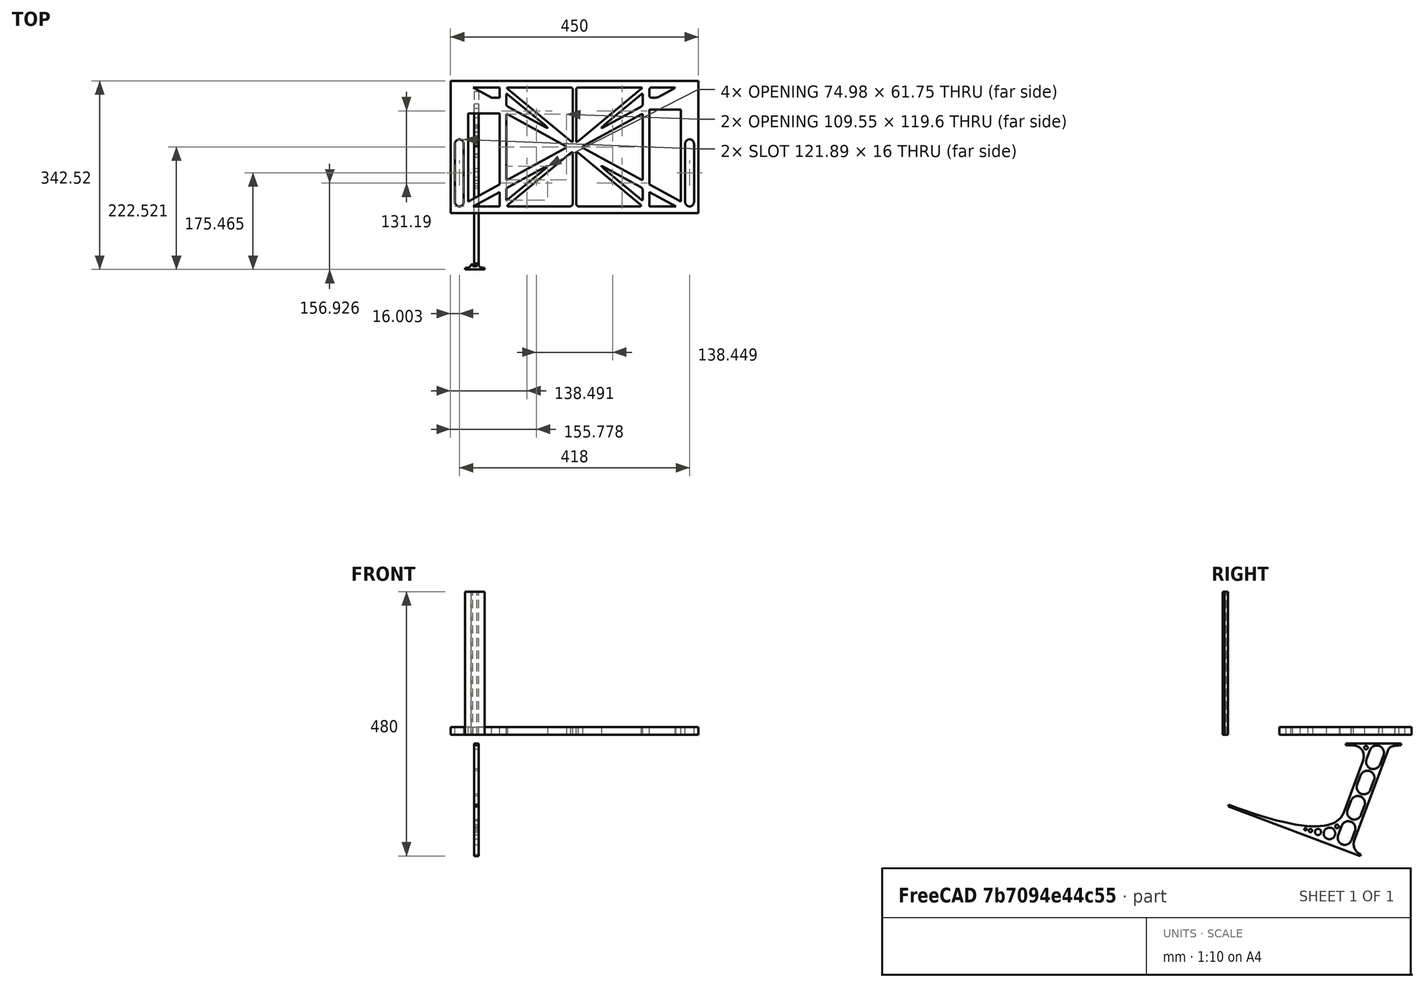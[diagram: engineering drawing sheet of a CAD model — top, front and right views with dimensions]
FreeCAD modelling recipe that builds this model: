
FCSTD DOCUMENT  (FreeCAD 0.19R0.19.2)
Label: laptopStand100
License: All rights reserved
LicenseURL: http://en.wikipedia.org/wiki/All_rights_reserved
objects: Sketcher::SketchObject×3, Part::Extrusion×3
note: 6 computed .brp shape members not serialized (recipe doc carries the construction recipe); baked Part::Feature solids carry a one-line shape summary decoded from their .brp

FEATURE [Sketcher::SketchObject] Sketch
  FullyConstrained = false
  sketch-geometry (276):
    g0: LineSegment StartX=-10.9272 StartY=-82.7794 StartZ=0 EndX=46.0728 EndY=-51.4823 EndZ=0
    g1: LineSegment StartX=366.073 StartY=-91.7794 StartZ=0 EndX=318.073 EndY=-65.424 EndZ=0
    g2: LineSegment StartX=-10.9272 StartY=77.3346 StartZ=0 EndX=-10.9272 EndY=-82.7794 EndZ=0
    g3: LineSegment StartX=375.073 StartY=-82.7794 StartZ=0 EndX=375.073 EndY=83.9235 EndZ=0
    g4: LineSegment StartX=-1.92719 StartY=-91.7794 StartZ=0 EndX=46.0728 EndY=-91.7794 EndZ=0
    g5: LineSegment StartX=318.073 StartY=83.9235 StartZ=0 EndX=318.073 EndY=-51.4823 EndZ=0
    g6: LineSegment StartX=318.073 StartY=-51.4823 StartZ=0 EndX=375.073 EndY=-82.7794 EndZ=0
    g7: LineSegment StartX=318.073 StartY=-65.424 StartZ=0 EndX=318.073 EndY=-91.7794 EndZ=0
    g8: LineSegment StartX=318.073 StartY=-91.7794 StartZ=0 EndX=366.073 EndY=-91.7794 EndZ=0
    g9: LineSegment StartX=46.0728 StartY=-65.424 StartZ=0 EndX=-1.92719 EndY=-91.7794 EndZ=0
    g10: LineSegment StartX=46.0728 StartY=-65.424 StartZ=0 EndX=46.0728 EndY=-91.7794 EndZ=0
    g11: LineSegment StartX=46.0728 StartY=77.3346 StartZ=0 EndX=46.0728 EndY=-51.4823 EndZ=0
    g12: LineSegment StartX=-42.9272 StartY=136.221 StartZ=0 EndX=-42.9272 EndY=-103.779 EndZ=0
    g13: LineSegment StartX=407.073 StartY=136.221 StartZ=0 EndX=407.073 EndY=-103.779 EndZ=0
    g14: ArcOfCircle CenterX=-26.9272 CenterY=22.1087 CenterZ=0 NormalX=0 NormalY=0 NormalZ=1 AngleXU=0 Radius=8 StartAngle=1e-16 EndAngle=3.14159
    g15: ArcOfCircle CenterX=-26.9272 CenterY=-83.7794 CenterZ=0 NormalX=0 NormalY=0 NormalZ=1 AngleXU=0 Radius=8 StartAngle=3.14159 EndAngle=6.28319
    g16: LineSegment StartX=-34.9272 StartY=22.1087 StartZ=0 EndX=-34.9272 EndY=-83.7794 EndZ=0
    g17: LineSegment StartX=-18.9272 StartY=22.1087 StartZ=0 EndX=-18.9272 EndY=-83.7794 EndZ=0
    g18: ArcOfCircle CenterX=391.073 CenterY=22.1087 CenterZ=0 NormalX=0 NormalY=0 NormalZ=1 AngleXU=0 Radius=8 StartAngle=-4.4e-15 EndAngle=3.14159
    g19: LineSegment StartX=399.073 StartY=22.1087 StartZ=0 EndX=399.073 EndY=-83.7794 EndZ=0
    g20: LineSegment StartX=383.073 StartY=22.1087 StartZ=0 EndX=383.073 EndY=-83.7794 EndZ=0
    g21: ArcOfCircle CenterX=391.073 CenterY=-83.7794 CenterZ=0 NormalX=0 NormalY=0 NormalZ=1 AngleXU=0 Radius=8 StartAngle=3.14159 EndAngle=6.28319
    g22: Circle CenterX=175.022 CenterY=27.0628 CenterZ=0 NormalX=0 NormalY=0 NormalZ=1 AngleXU=0 Radius=1
    g23: Circle CenterX=179.022 CenterY=24.8665 CenterZ=0 NormalX=0 NormalY=0 NormalZ=1 AngleXU=0 Radius=1
    g24: Circle CenterX=179.022 CenterY=27.0628 CenterZ=0 NormalX=0 NormalY=0 NormalZ=1 AngleXU=0 Radius=1
    g25: BSplineCurve PolesCount=3 KnotsCount=2 Degree=2 IsPeriodic=0
    g26: GeomPoint X=175.022 Y=27.0628 Z=0
    g27: GeomPoint X=179.022 Y=27.0628 Z=0
    g28: Circle CenterX=189.124 CenterY=27.0628 CenterZ=0 NormalX=0 NormalY=0 NormalZ=1 AngleXU=0 Radius=1
    g29: Circle CenterX=185.124 CenterY=24.8665 CenterZ=0 NormalX=0 NormalY=0 NormalZ=1 AngleXU=0 Radius=1
    g30: Circle CenterX=185.124 CenterY=27.0628 CenterZ=0 NormalX=0 NormalY=0 NormalZ=1 AngleXU=0 Radius=1
    g31: BSplineCurve PolesCount=3 KnotsCount=2 Degree=2 IsPeriodic=0
    g32: GeomPoint X=189.124 Y=27.0628 Z=0
    g33: GeomPoint X=185.124 Y=27.0628 Z=0
    g34: Circle CenterX=175.022 CenterY=5.37834 CenterZ=0 NormalX=0 NormalY=0 NormalZ=1 AngleXU=0 Radius=1
    g35: Circle CenterX=179.022 CenterY=7.57463 CenterZ=0 NormalX=0 NormalY=0 NormalZ=1 AngleXU=0 Radius=1
    g36: Circle CenterX=179.022 CenterY=5.34704 CenterZ=0 NormalX=0 NormalY=0 NormalZ=1 AngleXU=0 Radius=1
    g37: BSplineCurve PolesCount=3 KnotsCount=2 Degree=2 IsPeriodic=0
    g38: GeomPoint X=175.022 Y=5.37834 Z=0
    g39: GeomPoint X=179.022 Y=5.34704 Z=0
    g40: Circle CenterX=189.124 CenterY=5.37834 CenterZ=0 NormalX=0 NormalY=0 NormalZ=1 AngleXU=0 Radius=1
    g41: Circle CenterX=185.124 CenterY=7.57463 CenterZ=0 NormalX=0 NormalY=0 NormalZ=1 AngleXU=0 Radius=1
    g42: Circle CenterX=185.124 CenterY=5.34704 CenterZ=0 NormalX=0 NormalY=0 NormalZ=1 AngleXU=0 Radius=1
    g43: BSplineCurve PolesCount=3 KnotsCount=2 Degree=2 IsPeriodic=0
    g44: GeomPoint X=189.124 Y=5.37834 Z=0
    g45: GeomPoint X=185.124 Y=5.34704 Z=0
    g46: Circle CenterX=165.871 CenterY=18.1458 CenterZ=0 NormalX=0 NormalY=0 NormalZ=1 AngleXU=0 Radius=1
    g47: Circle CenterX=169.377 CenterY=16.2206 CenterZ=0 NormalX=0 NormalY=0 NormalZ=1 AngleXU=0 Radius=1
    g48: Circle CenterX=165.871 CenterY=14.2954 CenterZ=0 NormalX=0 NormalY=0 NormalZ=1 AngleXU=0 Radius=1
    g49: BSplineCurve PolesCount=3 KnotsCount=2 Degree=2 IsPeriodic=0
    g50: GeomPoint X=165.871 Y=18.1458 Z=0
    g51: GeomPoint X=165.871 Y=14.2954 Z=0
    g52: Circle CenterX=198.275 CenterY=18.1458 CenterZ=0 NormalX=0 NormalY=0 NormalZ=1 AngleXU=0 Radius=1
    g53: Circle CenterX=194.768 CenterY=16.2206 CenterZ=0 NormalX=0 NormalY=0 NormalZ=1 AngleXU=0 Radius=1
    g54: Circle CenterX=198.275 CenterY=14.2954 CenterZ=0 NormalX=0 NormalY=0 NormalZ=1 AngleXU=0 Radius=1
    g55: BSplineCurve PolesCount=3 KnotsCount=2 Degree=2 IsPeriodic=0
    g56: GeomPoint X=198.275 Y=18.1458 Z=0
    g57: GeomPoint X=198.275 Y=14.2954 Z=0
    g58: LineSegment StartX=407.073 StartY=-103.779 StartZ=0 EndX=-42.9272 EndY=-103.779 EndZ=0
    g59: LineSegment StartX=407.073 StartY=136.221 StartZ=0 EndX=-42.9272 EndY=136.221 EndZ=0
    g60: LineSegment StartX=46.0728 StartY=77.3346 StartZ=0 EndX=-10.9272 EndY=77.3346 EndZ=0
    g61: LineSegment StartX=46.0728 StartY=105.865 StartZ=0 EndX=31.5028 EndY=105.865 EndZ=0
    g62: LineSegment StartX=46.0728 StartY=124.221 StartZ=0 EndX=46.0728 EndY=105.865 EndZ=0
    g63: LineSegment StartX=-1.92719 StartY=124.221 StartZ=0 EndX=31.5028 EndY=105.865 EndZ=0
    g64: LineSegment StartX=46.0728 StartY=124.221 StartZ=0 EndX=-1.92719 EndY=124.221 EndZ=0
    g65: LineSegment StartX=318.073 StartY=83.9235 StartZ=0 EndX=375.073 EndY=83.9235 EndZ=0
    g66: Circle CenterX=125.607 CenterY=54.1951 CenterZ=0 NormalX=0 NormalY=0 NormalZ=1 AngleXU=0 Radius=1
    g67: Circle CenterX=139.632 CenterY=46.4944 CenterZ=0 NormalX=0 NormalY=0 NormalZ=1 AngleXU=0 Radius=1
    g68: Circle CenterX=127.326 CenterY=56.7187 CenterZ=0 NormalX=0 NormalY=0 NormalZ=1 AngleXU=0 Radius=1
    g69: BSplineCurve PolesCount=3 KnotsCount=2 Degree=2 IsPeriodic=0
    g70: GeomPoint X=125.607 Y=54.1951 Z=0
    g71: GeomPoint X=127.326 Y=56.7187 Z=0
    g72: Circle CenterX=236.821 CenterY=56.7187 CenterZ=0 NormalX=0 NormalY=0 NormalZ=1 AngleXU=0 Radius=1
    g73: Circle CenterX=224.513 CenterY=46.4944 CenterZ=0 NormalX=0 NormalY=0 NormalZ=1 AngleXU=0 Radius=1
    g74: Circle CenterX=238.538 CenterY=54.1951 CenterZ=0 NormalX=0 NormalY=0 NormalZ=1 AngleXU=0 Radius=1
    g75: BSplineCurve PolesCount=3 KnotsCount=2 Degree=2 IsPeriodic=0
    g76: GeomPoint X=236.821 Y=56.7187 Z=0
    g77: GeomPoint X=238.538 Y=54.1951 Z=0
    g78: Circle CenterX=238.538 CenterY=-21.7539 CenterZ=0 NormalX=0 NormalY=0 NormalZ=1 AngleXU=0 Radius=1
    g79: Circle CenterX=224.513 CenterY=-14.0532 CenterZ=0 NormalX=0 NormalY=0 NormalZ=1 AngleXU=0 Radius=1
    g80: Circle CenterX=236.821 CenterY=-24.2775 CenterZ=0 NormalX=0 NormalY=0 NormalZ=1 AngleXU=0 Radius=1
    g81: BSplineCurve PolesCount=3 KnotsCount=2 Degree=2 IsPeriodic=0
    g82: GeomPoint X=238.538 Y=-21.7539 Z=0
    g83: GeomPoint X=236.821 Y=-24.2775 Z=0
    g84: Circle CenterX=125.607 CenterY=-21.7539 CenterZ=0 NormalX=0 NormalY=0 NormalZ=1 AngleXU=0 Radius=1
    g85: Circle CenterX=139.632 CenterY=-14.0532 CenterZ=0 NormalX=0 NormalY=0 NormalZ=1 AngleXU=0 Radius=1
    g86: Circle CenterX=127.325 CenterY=-24.2775 CenterZ=0 NormalX=0 NormalY=0 NormalZ=1 AngleXU=0 Radius=1
    g87: BSplineCurve PolesCount=3 KnotsCount=2 Degree=2 IsPeriodic=0
    g88: GeomPoint X=125.607 Y=-21.7539 Z=0
    g89: GeomPoint X=127.325 Y=-24.2775 Z=0
    g90: Circle CenterX=302.996 CenterY=111.695 CenterZ=0 NormalX=0 NormalY=0 NormalZ=1 AngleXU=0 Radius=1
    g91: Circle CenterX=306.073 CenterY=114.251 CenterZ=0 NormalX=0 NormalY=0 NormalZ=1 AngleXU=0 Radius=1
    g92: Circle CenterX=306.073 CenterY=110.251 CenterZ=0 NormalX=0 NormalY=0 NormalZ=1 AngleXU=0 Radius=1
    g93: BSplineCurve PolesCount=3 KnotsCount=2 Degree=2 IsPeriodic=0
    g94: GeomPoint X=302.996 Y=111.695 Z=0
    g95: GeomPoint X=306.073 Y=110.251 Z=0
    g96: Circle CenterX=306.073 CenterY=95.2763 CenterZ=0 NormalX=0 NormalY=0 NormalZ=1 AngleXU=0 Radius=1
    g97: Circle CenterX=306.073 CenterY=91.2763 CenterZ=0 NormalX=0 NormalY=0 NormalZ=1 AngleXU=0 Radius=1
    g98: Circle CenterX=302.567 CenterY=89.3511 CenterZ=0 NormalX=0 NormalY=0 NormalZ=1 AngleXU=0 Radius=1
    g99: BSplineCurve PolesCount=3 KnotsCount=2 Degree=2 IsPeriodic=0
    g100: GeomPoint X=306.073 Y=95.2763 Z=0
    g101: GeomPoint X=302.567 Y=89.3511 Z=0
    g102: LineSegment StartX=306.073 StartY=110.251 StartZ=0 EndX=306.073 EndY=95.2763 EndZ=0
    g103: LineSegment StartX=302.996 StartY=111.695 StartZ=0 EndX=236.821 EndY=56.7187 EndZ=0
    g104: LineSegment StartX=238.538 StartY=54.1951 StartZ=0 EndX=302.567 EndY=89.3511 EndZ=0
    g105: Circle CenterX=61.1496 CenterY=111.695 CenterZ=0 NormalX=0 NormalY=0 NormalZ=1 AngleXU=0 Radius=1
    g106: Circle CenterX=58.0728 CenterY=114.251 CenterZ=0 NormalX=0 NormalY=0 NormalZ=1 AngleXU=0 Radius=1
    g107: Circle CenterX=58.0728 CenterY=110.251 CenterZ=0 NormalX=0 NormalY=0 NormalZ=1 AngleXU=0 Radius=1
    g108: BSplineCurve PolesCount=3 KnotsCount=2 Degree=2 IsPeriodic=0
    g109: GeomPoint X=61.1496 Y=111.695 Z=0
    g110: GeomPoint X=58.0728 Y=110.251 Z=0
    g111: Circle CenterX=61.5791 CenterY=89.3511 CenterZ=0 NormalX=0 NormalY=0 NormalZ=1 AngleXU=0 Radius=1
    g112: Circle CenterX=58.0728 CenterY=91.2763 CenterZ=0 NormalX=0 NormalY=0 NormalZ=1 AngleXU=0 Radius=1
    g113: Circle CenterX=58.0728 CenterY=95.2763 CenterZ=0 NormalX=0 NormalY=0 NormalZ=1 AngleXU=0 Radius=1
    g114: BSplineCurve PolesCount=3 KnotsCount=2 Degree=2 IsPeriodic=0
    g115: GeomPoint X=61.5791 Y=89.3511 Z=0
    g116: GeomPoint X=58.0728 Y=95.2763 Z=0
    g117: LineSegment StartX=58.0728 StartY=110.251 StartZ=0 EndX=58.0728 EndY=95.2763 EndZ=0
    g118: LineSegment StartX=61.1496 StartY=111.695 StartZ=0 EndX=127.326 EndY=56.7187 EndZ=0
    g119: LineSegment StartX=125.607 StartY=54.1951 StartZ=0 EndX=61.5791 EndY=89.3511 EndZ=0
    g120: Circle CenterX=61.5791 CenterY=-56.9099 CenterZ=0 NormalX=0 NormalY=0 NormalZ=1 AngleXU=0 Radius=1
    g121: Circle CenterX=58.0728 CenterY=-58.8351 CenterZ=0 NormalX=0 NormalY=0 NormalZ=1 AngleXU=0 Radius=1
    g122: Circle CenterX=58.0728 CenterY=-62.8351 CenterZ=0 NormalX=0 NormalY=0 NormalZ=1 AngleXU=0 Radius=1
    g123: BSplineCurve PolesCount=3 KnotsCount=2 Degree=2 IsPeriodic=0
    g124: GeomPoint X=61.5791 Y=-56.9099 Z=0
    g125: GeomPoint X=58.0728 Y=-62.8351 Z=0
    g126: Circle CenterX=58.0728 CenterY=-77.8102 CenterZ=0 NormalX=0 NormalY=0 NormalZ=1 AngleXU=0 Radius=1
    g127: Circle CenterX=58.0728 CenterY=-81.8102 CenterZ=0 NormalX=0 NormalY=0 NormalZ=1 AngleXU=0 Radius=1
    g128: Circle CenterX=61.1496 CenterY=-79.2541 CenterZ=0 NormalX=0 NormalY=0 NormalZ=1 AngleXU=0 Radius=1
    g129: BSplineCurve PolesCount=3 KnotsCount=2 Degree=2 IsPeriodic=0
    g130: GeomPoint X=58.0728 Y=-77.8102 Z=0
    g131: GeomPoint X=61.1496 Y=-79.2541 Z=0
    g132: LineSegment StartX=58.0728 StartY=-62.8351 StartZ=0 EndX=58.0728 EndY=-77.8102 EndZ=0
    g133: LineSegment StartX=61.1496 StartY=-79.2541 StartZ=0 EndX=127.325 EndY=-24.2775 EndZ=0
    g134: LineSegment StartX=125.607 StartY=-21.7539 StartZ=0 EndX=61.5791 EndY=-56.9099 EndZ=0
    g135: Circle CenterX=302.567 CenterY=-56.9099 CenterZ=0 NormalX=0 NormalY=0 NormalZ=1 AngleXU=0 Radius=1
    g136: Circle CenterX=306.073 CenterY=-58.8351 CenterZ=0 NormalX=0 NormalY=0 NormalZ=1 AngleXU=0 Radius=1
    g137: Circle CenterX=306.073 CenterY=-62.8351 CenterZ=0 NormalX=0 NormalY=0 NormalZ=1 AngleXU=0 Radius=1
    g138: BSplineCurve PolesCount=3 KnotsCount=2 Degree=2 IsPeriodic=0
    g139: GeomPoint X=302.567 Y=-56.9099 Z=0
    g140: GeomPoint X=306.073 Y=-62.8351 Z=0
    g141: Circle CenterX=302.996 CenterY=-79.2541 CenterZ=0 NormalX=0 NormalY=0 NormalZ=1 AngleXU=0 Radius=1
    g142: Circle CenterX=306.073 CenterY=-81.8102 CenterZ=0 NormalX=0 NormalY=0 NormalZ=1 AngleXU=0 Radius=1
    g143: Circle CenterX=306.073 CenterY=-77.8102 CenterZ=0 NormalX=0 NormalY=0 NormalZ=1 AngleXU=0 Radius=1
    g144: BSplineCurve PolesCount=3 KnotsCount=2 Degree=2 IsPeriodic=0
    g145: GeomPoint X=302.996 Y=-79.2541 Z=0
    g146: GeomPoint X=306.073 Y=-77.8102 Z=0
    g147: LineSegment StartX=306.073 StartY=-62.8351 StartZ=0 EndX=306.073 EndY=-77.8102 EndZ=0
    g148: LineSegment StartX=302.996 StartY=-79.2541 StartZ=0 EndX=236.821 EndY=-24.2775 EndZ=0
    g149: LineSegment StartX=238.538 StartY=-21.7539 StartZ=0 EndX=302.567 EndY=-56.9099 EndZ=0
    g150: Circle CenterX=61.6457 CenterY=-88.8112 CenterZ=0 NormalX=0 NormalY=0 NormalZ=1 AngleXU=0 Radius=1
    g151: Circle CenterX=58.0728 CenterY=-91.7794 CenterZ=0 NormalX=0 NormalY=0 NormalZ=1 AngleXU=0 Radius=1
    g152: Circle CenterX=63.9135 CenterY=-91.7794 CenterZ=0 NormalX=0 NormalY=0 NormalZ=1 AngleXU=0 Radius=1
    g153: BSplineCurve PolesCount=3 KnotsCount=2 Degree=2 IsPeriodic=0
    g154: GeomPoint X=61.6457 Y=-88.8112 Z=0
    g155: GeomPoint X=63.9135 Y=-91.7794 Z=0
    g156: Circle CenterX=179.022 CenterY=-85.8163 CenterZ=0 NormalX=0 NormalY=0 NormalZ=1 AngleXU=0 Radius=1
    g157: Circle CenterX=179.022 CenterY=-91.7794 CenterZ=0 NormalX=0 NormalY=0 NormalZ=1 AngleXU=0 Radius=1
    g158: Circle CenterX=171.895 CenterY=-91.7794 CenterZ=0 NormalX=0 NormalY=0 NormalZ=1 AngleXU=0 Radius=1
    g159: BSplineCurve PolesCount=3 KnotsCount=2 Degree=2 IsPeriodic=0
    g160: GeomPoint X=179.022 Y=-85.8163 Z=0
    g161: GeomPoint X=171.895 Y=-91.7794 Z=0
    g162: Circle CenterX=185.124 CenterY=-86.2028 CenterZ=0 NormalX=0 NormalY=0 NormalZ=1 AngleXU=0 Radius=1
    g163: Circle CenterX=185.124 CenterY=-91.7794 CenterZ=0 NormalX=0 NormalY=0 NormalZ=1 AngleXU=0 Radius=1
    g164: Circle CenterX=191.747 CenterY=-91.7794 CenterZ=0 NormalX=0 NormalY=0 NormalZ=1 AngleXU=0 Radius=1
    g165: BSplineCurve PolesCount=3 KnotsCount=2 Degree=2 IsPeriodic=0
    g166: GeomPoint X=185.124 Y=-86.2028 Z=0
    g167: GeomPoint X=191.747 Y=-91.7794 Z=0
    g168: Circle CenterX=299.888 CenterY=-86.6413 CenterZ=0 NormalX=0 NormalY=0 NormalZ=1 AngleXU=0 Radius=1
    g169: Circle CenterX=306.073 CenterY=-91.7794 CenterZ=0 NormalX=0 NormalY=0 NormalZ=1 AngleXU=0 Radius=1
    g170: Circle CenterX=298.776 CenterY=-91.7794 CenterZ=0 NormalX=0 NormalY=0 NormalZ=1 AngleXU=0 Radius=1
    g171: BSplineCurve PolesCount=3 KnotsCount=2 Degree=2 IsPeriodic=0
    g172: GeomPoint X=299.888 Y=-86.6413 Z=0
    g173: GeomPoint X=298.776 Y=-91.7794 Z=0
    g174: LineSegment StartX=189.124 StartY=5.37834 StartZ=0 EndX=299.888 EndY=-86.6413 EndZ=0
    g175: LineSegment StartX=298.776 StartY=-91.7794 StartZ=0 EndX=191.747 EndY=-91.7794 EndZ=0
    g176: LineSegment StartX=185.124 StartY=-86.2028 StartZ=0 EndX=185.124 EndY=5.34704 EndZ=0
    g177: LineSegment StartX=179.022 StartY=5.34704 StartZ=0 EndX=179.022 EndY=-85.8163 EndZ=0
    g178: LineSegment StartX=171.895 StartY=-91.7794 StartZ=0 EndX=63.9135 EndY=-91.7794 EndZ=0
    g179: LineSegment StartX=61.6457 StartY=-88.8112 StartZ=0 EndX=175.022 EndY=5.37834 EndZ=0
    g180: Circle CenterX=302.073 CenterY=124.221 CenterZ=0 NormalX=0 NormalY=0 NormalZ=1 AngleXU=0 Radius=1
    g181: Circle CenterX=306.073 CenterY=124.221 CenterZ=0 NormalX=0 NormalY=0 NormalZ=1 AngleXU=0 Radius=1
    g182: Circle CenterX=302.996 CenterY=121.665 CenterZ=0 NormalX=0 NormalY=0 NormalZ=1 AngleXU=0 Radius=1
    g183: BSplineCurve PolesCount=3 KnotsCount=2 Degree=2 IsPeriodic=0
    g184: GeomPoint X=302.073 Y=124.221 Z=0
    g185: GeomPoint X=302.996 Y=121.665 Z=0
    g186: Circle CenterX=189.124 CenterY=124.221 CenterZ=0 NormalX=0 NormalY=0 NormalZ=1 AngleXU=0 Radius=1
    g187: Circle CenterX=185.124 CenterY=124.221 CenterZ=0 NormalX=0 NormalY=0 NormalZ=1 AngleXU=0 Radius=1
    g188: Circle CenterX=185.124 CenterY=120.221 CenterZ=0 NormalX=0 NormalY=0 NormalZ=1 AngleXU=0 Radius=1
    g189: BSplineCurve PolesCount=3 KnotsCount=2 Degree=2 IsPeriodic=0
    g190: GeomPoint X=189.124 Y=124.221 Z=0
    g191: GeomPoint X=185.124 Y=120.221 Z=0
    g192: Circle CenterX=175.022 CenterY=124.221 CenterZ=0 NormalX=0 NormalY=0 NormalZ=1 AngleXU=0 Radius=1
    g193: Circle CenterX=179.022 CenterY=124.221 CenterZ=0 NormalX=0 NormalY=0 NormalZ=1 AngleXU=0 Radius=1
    g194: Circle CenterX=179.022 CenterY=120.221 CenterZ=0 NormalX=0 NormalY=0 NormalZ=1 AngleXU=0 Radius=1
    g195: BSplineCurve PolesCount=3 KnotsCount=2 Degree=2 IsPeriodic=0
    g196: GeomPoint X=175.022 Y=124.221 Z=0
    g197: GeomPoint X=179.022 Y=120.221 Z=0
    g198: Circle CenterX=62.0728 CenterY=124.221 CenterZ=0 NormalX=0 NormalY=0 NormalZ=1 AngleXU=0 Radius=1
    g199: Circle CenterX=58.0728 CenterY=124.221 CenterZ=0 NormalX=0 NormalY=0 NormalZ=1 AngleXU=0 Radius=1
    g200: Circle CenterX=61.1496 CenterY=121.665 CenterZ=0 NormalX=0 NormalY=0 NormalZ=1 AngleXU=0 Radius=1
    g201: BSplineCurve PolesCount=3 KnotsCount=2 Degree=2 IsPeriodic=0
    g202: GeomPoint X=62.0728 Y=124.221 Z=0
    g203: GeomPoint X=61.1496 Y=121.665 Z=0
    g204: LineSegment StartX=62.0728 StartY=124.221 StartZ=0 EndX=175.022 EndY=124.221 EndZ=0
    g205: LineSegment StartX=179.022 StartY=120.221 StartZ=0 EndX=179.022 EndY=27.0628 EndZ=0
    g206: LineSegment StartX=185.124 StartY=27.0628 StartZ=0 EndX=185.124 EndY=120.221 EndZ=0
    g207: LineSegment StartX=189.124 StartY=124.221 StartZ=0 EndX=302.073 EndY=124.221 EndZ=0
    g208: LineSegment StartX=302.996 StartY=121.665 StartZ=0 EndX=189.124 EndY=27.0628 EndZ=0
    g209: LineSegment StartX=175.022 StartY=27.0628 StartZ=0 EndX=61.1496 EndY=121.665 EndZ=0
    g210: Circle CenterX=61.5791 CenterY=75.4095 CenterZ=0 NormalX=0 NormalY=0 NormalZ=1 AngleXU=0 Radius=1
    g211: Circle CenterX=58.0728 CenterY=77.3346 CenterZ=0 NormalX=0 NormalY=0 NormalZ=1 AngleXU=0 Radius=1
    g212: Circle CenterX=58.0728 CenterY=73.3346 CenterZ=0 NormalX=0 NormalY=0 NormalZ=1 AngleXU=0 Radius=1
    g213: BSplineCurve PolesCount=3 KnotsCount=2 Degree=2 IsPeriodic=0
    g214: GeomPoint X=61.5791 Y=75.4095 Z=0
    g215: GeomPoint X=58.0728 Y=73.3346 Z=0
    g216: Circle CenterX=58.0728 CenterY=-40.8935 CenterZ=0 NormalX=0 NormalY=0 NormalZ=1 AngleXU=0 Radius=1
    g217: Circle CenterX=58.0728 CenterY=-44.8935 CenterZ=0 NormalX=0 NormalY=0 NormalZ=1 AngleXU=0 Radius=1
    g218: Circle CenterX=61.5791 CenterY=-42.9683 CenterZ=0 NormalX=0 NormalY=0 NormalZ=1 AngleXU=0 Radius=1
    g219: BSplineCurve PolesCount=3 KnotsCount=2 Degree=2 IsPeriodic=0
    g220: GeomPoint X=58.0728 Y=-40.8935 Z=0
    g221: GeomPoint X=61.5791 Y=-42.9683 Z=0
    g222: LineSegment StartX=61.5791 StartY=-42.9683 StartZ=0 EndX=165.871 EndY=14.2954 EndZ=0
    g223: LineSegment StartX=165.871 StartY=18.1458 StartZ=0 EndX=61.5791 EndY=75.4095 EndZ=0
    g224: LineSegment StartX=58.0728 StartY=73.3346 StartZ=0 EndX=58.0728 EndY=-40.8935 EndZ=0
    g225: Circle CenterX=302.567 CenterY=-42.9683 CenterZ=0 NormalX=0 NormalY=0 NormalZ=1 AngleXU=0 Radius=1
    g226: Circle CenterX=306.073 CenterY=-44.8935 CenterZ=0 NormalX=0 NormalY=0 NormalZ=1 AngleXU=0 Radius=1
    g227: Circle CenterX=306.073 CenterY=-40.8935 CenterZ=0 NormalX=0 NormalY=0 NormalZ=1 AngleXU=0 Radius=1
    g228: BSplineCurve PolesCount=3 KnotsCount=2 Degree=2 IsPeriodic=0
    g229: GeomPoint X=302.567 Y=-42.9683 Z=0
    g230: GeomPoint X=306.073 Y=-40.8935 Z=0
    g231: Circle CenterX=306.073 CenterY=73.3346 CenterZ=0 NormalX=0 NormalY=0 NormalZ=1 AngleXU=0 Radius=1
    g232: Circle CenterX=306.073 CenterY=77.3346 CenterZ=0 NormalX=0 NormalY=0 NormalZ=1 AngleXU=0 Radius=1
    g233: Circle CenterX=302.567 CenterY=75.4095 CenterZ=0 NormalX=0 NormalY=0 NormalZ=1 AngleXU=0 Radius=1
    g234: BSplineCurve PolesCount=3 KnotsCount=2 Degree=2 IsPeriodic=0
    g235: GeomPoint X=306.073 Y=73.3346 Z=0
    g236: GeomPoint X=302.567 Y=75.4095 Z=0
    g237: LineSegment StartX=302.567 StartY=-42.9683 StartZ=0 EndX=198.275 EndY=14.2954 EndZ=0
    g238: LineSegment StartX=198.275 StartY=18.1458 StartZ=0 EndX=302.567 EndY=75.4095 EndZ=0
    g239: LineSegment StartX=306.073 StartY=73.3346 StartZ=0 EndX=306.073 EndY=-40.8935 EndZ=0
    g240: LineSegment StartX=322.073 StartY=105.865 StartZ=0 EndX=328.643 EndY=105.865 EndZ=0
    g241: LineSegment StartX=318.073 StartY=120.221 StartZ=0 EndX=318.073 EndY=109.865 EndZ=0
    g242: LineSegment StartX=336.157 StartY=107.779 StartZ=0 EndX=362.567 EndY=122.294 EndZ=0
    g243: Circle CenterX=362.073 CenterY=124.221 CenterZ=0 NormalX=0 NormalY=0 NormalZ=1 AngleXU=0 Radius=1
    g244: Circle CenterX=366.073 CenterY=124.221 CenterZ=0 NormalX=0 NormalY=0 NormalZ=1 AngleXU=0 Radius=1
    g245: Circle CenterX=362.567 CenterY=122.294 CenterZ=0 NormalX=0 NormalY=0 NormalZ=1 AngleXU=0 Radius=1
    g246: BSplineCurve PolesCount=3 KnotsCount=2 Degree=2 IsPeriodic=0
    g247: GeomPoint X=362.073 Y=124.221 Z=0
    g248: GeomPoint X=362.567 Y=122.294 Z=0
    g249: Circle CenterX=322.073 CenterY=124.221 CenterZ=0 NormalX=0 NormalY=0 NormalZ=1 AngleXU=0 Radius=1
    g250: Circle CenterX=318.073 CenterY=124.221 CenterZ=0 NormalX=0 NormalY=0 NormalZ=1 AngleXU=0 Radius=1
    g251: Circle CenterX=318.073 CenterY=120.221 CenterZ=0 NormalX=0 NormalY=0 NormalZ=1 AngleXU=0 Radius=1
    g252: BSplineCurve PolesCount=3 KnotsCount=2 Degree=2 IsPeriodic=0
    g253: GeomPoint X=322.073 Y=124.221 Z=0
    g254: GeomPoint X=318.073 Y=120.221 Z=0
    g255: Circle CenterX=322.073 CenterY=105.865 CenterZ=0 NormalX=0 NormalY=0 NormalZ=1 AngleXU=0 Radius=1
    g256: Circle CenterX=318.073 CenterY=105.865 CenterZ=0 NormalX=0 NormalY=0 NormalZ=1 AngleXU=0 Radius=1
    g257: Circle CenterX=318.073 CenterY=109.865 CenterZ=0 NormalX=0 NormalY=0 NormalZ=1 AngleXU=0 Radius=1
    g258: BSplineCurve PolesCount=3 KnotsCount=2 Degree=2 IsPeriodic=0
    g259: GeomPoint X=322.073 Y=105.865 Z=0
    g260: GeomPoint X=318.073 Y=109.865 Z=0
    g261: Circle CenterX=336.157 CenterY=107.779 CenterZ=0 NormalX=0 NormalY=0 NormalZ=1 AngleXU=0 Radius=1
    g262: Circle CenterX=332.651 CenterY=105.853 CenterZ=0 NormalX=0 NormalY=0 NormalZ=1 AngleXU=0 Radius=1
    g263: Circle CenterX=328.643 CenterY=105.865 CenterZ=0 NormalX=0 NormalY=0 NormalZ=1 AngleXU=0 Radius=1
    g264: BSplineCurve PolesCount=3 KnotsCount=2 Degree=2 IsPeriodic=0
    g265: GeomPoint X=336.157 Y=107.779 Z=0
    g266: GeomPoint X=328.643 Y=105.865 Z=0
    g267: LineSegment StartX=322.073 StartY=124.221 StartZ=0 EndX=362.073 EndY=124.221 EndZ=0
    g268: LineSegment StartX=319.04 StartY=85.0727 StartZ=0 EndX=323.589 EndY=85.0727 EndZ=0
    g269: LineSegment StartX=317.109 StartY=83.1843 StartZ=0 EndX=317.109 EndY=78.2919 EndZ=0
    g270: LineSegment StartX=374.539 StartY=84.6841 StartZ=0 EndX=370.161 EndY=84.6841 EndZ=0
    g271: LineSegment StartX=376.298 StartY=83.0104 StartZ=0 EndX=376.298 EndY=79.2337 EndZ=0
    g272: LineSegment StartX=375.914 StartY=-81.9707 StartZ=0 EndX=375.914 EndY=-78.5374 EndZ=0
    g273: LineSegment StartX=373.94 StartY=-83.3011 StartZ=0 EndX=369.219 EndY=-80.8978 EndZ=0
    g274: LineSegment StartX=319.222 StartY=-53.6889 StartZ=0 EndX=323.385 EndY=-56.0922 EndZ=0
    g275: LineSegment StartX=316.982 StartY=-49.2086 StartZ=0 EndX=316.982 EndY=-42.7283 EndZ=0
  constraints (455):
    c: Horizontal(g4)
    c: Coincident(g5,g6)
    c: Coincident(g7,g1)
    c: Tangent(g5,g7)
    c: Coincident(g10,g9)
    c: Coincident(g0,g11)
    c: Block(g6)
    c: Block(g3)
    c: Block(g1)
    c: Block(g7)
    c: Block(g10)
    c: Block(g9)
    c: Block(g0)
    c: Block(g2)
    c: Block(g8)
    c: Block(g4)
    c: Vertical(g12)
    c: Vertical(g13)
    c: Block(g13)
    c: Block(g12)
    c: Tangent(g14,g17) = 1.5708
    c: Tangent(g14,g16) = -1.5708
    c: Tangent(g16,g15) = -1.5708
    c: Tangent(g17,g15) = 1.5708
    c: Vertical(g16)
    c: Equal(g14,g15)
    c: Block(g17)
    c: Block(g16)
    c: Tangent(g18,g19) = 1.5708
    c: Tangent(g19,g21) = 1.5708
    c: Equal(g18,g21)
    c: Coincident(g20,g18)
    c: Coincident(g20,g21)
    c: Block(g19)
    c: Block(g20)
    c: Weight(g22) = 1
    c: Equal(g22,g23)
    c: Equal(g22,g24)
    c: InternalAlignment(g22,g25)
    c: InternalAlignment(g23,g25)
    c: InternalAlignment(g24,g25)
    c: InternalAlignment(g26,g25)
    c: InternalAlignment(g27,g25)
    c: Weight(g28) = 1
    c: Equal(g28,g29)
    c: Equal(g28,g30)
    c: InternalAlignment(g28,g31)
    c: InternalAlignment(g29,g31)
    c: InternalAlignment(g30,g31)
    c: InternalAlignment(g32,g31)
    c: InternalAlignment(g33,g31)
    c: Block(g31)
    c: Block(g25)
    c: Weight(g34) = 1
    c: Equal(g34,g35)
    c: Equal(g34,g36)
    c: InternalAlignment(g34,g37)
    c: InternalAlignment(g35,g37)
    c: InternalAlignment(g36,g37)
    c: InternalAlignment(g38,g37)
    c: InternalAlignment(g39,g37)
    c: Weight(g40) = 1
    c: Equal(g40,g41)
    c: Equal(g40,g42)
    c: InternalAlignment(g40,g43)
    c: InternalAlignment(g41,g43)
    c: InternalAlignment(g42,g43)
    c: InternalAlignment(g44,g43)
    c: InternalAlignment(g45,g43)
    c: Block(g43)
    c: Block(g37)
    c: Weight(g46) = 1
    c: Equal(g46,g47)
    c: Equal(g46,g48)
    c: InternalAlignment(g46,g49)
    c: InternalAlignment(g47,g49)
    c: InternalAlignment(g48,g49)
    c: InternalAlignment(g50,g49)
    c: InternalAlignment(g51,g49)
    c: Weight(g52) = 1
    c: Equal(g52,g53)
    c: Equal(g52,g54)
    c: InternalAlignment(g52,g55)
    c: InternalAlignment(g53,g55)
    c: InternalAlignment(g54,g55)
    c: InternalAlignment(g56,g55)
    c: InternalAlignment(g57,g55)
    c: Block(g49)
    c: Block(g55)
    c: Coincident(g58,g13)
    c: Coincident(g58,g12)
    c: Horizontal(g58)
    c: Distance(g58) = 450
    c: Coincident(g59,g13)
    c: Coincident(g59,g12)
    c: Horizontal(g59)
    c: Horizontal(g60)
    c: Coincident(g11,g60)
    c: Horizontal(g61)
    c: Vertical(g62)
    c: Block(g62)
    c: Block(g61)
    c: Block(g60)
    c: Distance(g62) = 18.3554
    c: Coincident(g64,g62)
    c: Coincident(g64,g63)
    c: Horizontal(g64)
    c: Block(g64)
    c: Block(g63)
    c: Coincident(g61,g63)
    c: Coincident(g2,g60)
    c: Coincident(g65,g5)
    c: Horizontal(g65)
    c: Block(g65)
    c: Coincident(g3,g65)
    c: Weight(g66) = 1
    c: Equal(g66,g67)
    c: Equal(g66,g68)
    c: InternalAlignment(g66,g69)
    c: InternalAlignment(g67,g69)
    c: InternalAlignment(g68,g69)
    c: InternalAlignment(g70,g69)
    c: InternalAlignment(g71,g69)
    c: Block(g69)
    c: Weight(g72) = 1
    c: Equal(g72,g73)
    c: Equal(g72,g74)
    c: InternalAlignment(g72,g75)
    c: InternalAlignment(g73,g75)
    c: InternalAlignment(g74,g75)
    c: InternalAlignment(g76,g75)
    c: InternalAlignment(g77,g75)
    c: Block(g75)
    c: Weight(g78) = 1
    c: Equal(g78,g79)
    c: Equal(g78,g80)
    c: InternalAlignment(g78,g81)
    c: InternalAlignment(g79,g81)
    c: InternalAlignment(g80,g81)
    c: InternalAlignment(g82,g81)
    c: InternalAlignment(g83,g81)
    c: Block(g81)
    c: Weight(g84) = 1
    c: Equal(g84,g85)
    c: Equal(g84,g86)
    c: InternalAlignment(g84,g87)
    c: InternalAlignment(g85,g87)
    c: InternalAlignment(g86,g87)
    c: InternalAlignment(g88,g87)
    c: InternalAlignment(g89,g87)
    c: Block(g87)
    c: Weight(g90) = 1
    c: Equal(g90,g91)
    c: Equal(g90,g92)
    c: InternalAlignment(g90,g93)
    c: InternalAlignment(g91,g93)
    c: InternalAlignment(g92,g93)
    c: InternalAlignment(g94,g93)
    c: InternalAlignment(g95,g93)
    c: Weight(g96) = 1
    c: Equal(g96,g97)
    c: Equal(g96,g98)
    c: InternalAlignment(g96,g99)
    c: InternalAlignment(g97,g99)
    c: InternalAlignment(g98,g99)
    c: InternalAlignment(g100,g99)
    c: InternalAlignment(g101,g99)
    c: Block(g93)
    c: Block(g99)
    c: Coincident(g102,g93)
    c: Coincident(g102,g99)
    c: Vertical(g102)
    c: Coincident(g103,g93)
    c: Coincident(g103,g75)
    c: Coincident(g104,g75)
    c: Coincident(g104,g99)
    c: Weight(g105) = 1
    c: Equal(g105,g106)
    c: Equal(g105,g107)
    c: InternalAlignment(g105,g108)
    c: InternalAlignment(g106,g108)
    c: InternalAlignment(g107,g108)
    c: InternalAlignment(g109,g108)
    c: InternalAlignment(g110,g108)
    c: Weight(g111) = 1
    c: Equal(g111,g112)
    c: Equal(g111,g113)
    c: InternalAlignment(g111,g114)
    c: InternalAlignment(g112,g114)
    c: InternalAlignment(g113,g114)
    c: InternalAlignment(g115,g114)
    c: InternalAlignment(g116,g114)
    c: Block(g108)
    c: Block(g114)
    c: Coincident(g117,g108)
    c: Coincident(g117,g114)
    c: Vertical(g117)
    c: Coincident(g118,g108)
    c: Coincident(g118,g69)
    c: Coincident(g119,g69)
    c: Coincident(g119,g114)
    c: Weight(g120) = 1
    c: Equal(g120,g121)
    c: Equal(g120,g122)
    c: InternalAlignment(g120,g123)
    c: InternalAlignment(g121,g123)
    c: InternalAlignment(g122,g123)
    c: InternalAlignment(g124,g123)
    c: InternalAlignment(g125,g123)
    c: Weight(g126) = 1
    c: Equal(g126,g127)
    c: Equal(g126,g128)
    c: InternalAlignment(g126,g129)
    c: InternalAlignment(g127,g129)
    c: InternalAlignment(g128,g129)
    c: InternalAlignment(g130,g129)
    c: InternalAlignment(g131,g129)
    c: Block(g123)
    c: Block(g129)
    c: Coincident(g132,g123)
    c: Coincident(g132,g129)
    c: Vertical(g132)
    c: Coincident(g133,g129)
    c: Coincident(g133,g87)
    c: Coincident(g134,g87)
    c: Coincident(g134,g123)
    c: Weight(g135) = 1
    c: Equal(g135,g136)
    c: Equal(g135,g137)
    c: InternalAlignment(g135,g138)
    c: InternalAlignment(g136,g138)
    c: InternalAlignment(g137,g138)
    c: InternalAlignment(g139,g138)
    c: InternalAlignment(g140,g138)
    c: Weight(g141) = 1
    c: Equal(g141,g142)
    c: Equal(g141,g143)
    c: InternalAlignment(g141,g144)
    c: InternalAlignment(g142,g144)
    c: InternalAlignment(g143,g144)
    c: InternalAlignment(g145,g144)
    c: InternalAlignment(g146,g144)
    c: Block(g138)
    c: Block(g144)
    c: Coincident(g147,g138)
    c: Coincident(g147,g144)
    c: Vertical(g147)
    c: Coincident(g148,g144)
    c: Coincident(g148,g81)
    c: Coincident(g149,g81)
    c: Coincident(g149,g138)
    c: Weight(g150) = 1
    c: Equal(g150,g151)
    c: Equal(g150,g152)
    c: InternalAlignment(g150,g153)
    c: InternalAlignment(g151,g153)
    c: InternalAlignment(g152,g153)
    c: InternalAlignment(g154,g153)
    c: InternalAlignment(g155,g153)
    c: Weight(g156) = 1
    c: Equal(g156,g157)
    c: Equal(g156,g158)
    c: InternalAlignment(g156,g159)
    c: InternalAlignment(g157,g159)
    c: InternalAlignment(g158,g159)
    c: InternalAlignment(g160,g159)
    c: InternalAlignment(g161,g159)
    c: Weight(g162) = 1
    c: Equal(g162,g163)
    c: Equal(g162,g164)
    c: InternalAlignment(g162,g165)
    c: InternalAlignment(g163,g165)
    c: InternalAlignment(g164,g165)
    c: InternalAlignment(g166,g165)
    c: InternalAlignment(g167,g165)
    c: Weight(g168) = 1
    c: Equal(g168,g169)
    c: Equal(g168,g170)
    c: InternalAlignment(g168,g171)
    c: InternalAlignment(g169,g171)
    c: InternalAlignment(g170,g171)
    c: InternalAlignment(g172,g171)
    c: InternalAlignment(g173,g171)
    c: Block(g171)
    c: Block(g165)
    c: Block(g159)
    c: Block(g153)
    c: Coincident(g174,g43)
    c: Coincident(g174,g171)
    c: Coincident(g175,g171)
    c: Coincident(g175,g165)
    c: Horizontal(g175)
    c: Coincident(g176,g165)
    c: Coincident(g176,g43)
    c: Vertical(g176)
    c: Coincident(g177,g37)
    c: Coincident(g177,g159)
    c: Vertical(g177)
    c: Coincident(g178,g159)
    c: Coincident(g178,g153)
    c: Horizontal(g178)
    c: Coincident(g179,g153)
    c: Coincident(g179,g37)
    c: Weight(g180) = 1
    c: Equal(g180,g181)
    c: Equal(g180,g182)
    c: InternalAlignment(g180,g183)
    c: InternalAlignment(g181,g183)
    c: InternalAlignment(g182,g183)
    c: InternalAlignment(g184,g183)
    c: InternalAlignment(g185,g183)
    c: Weight(g186) = 1
    c: Equal(g186,g187)
    c: Equal(g186,g188)
    c: InternalAlignment(g186,g189)
    c: InternalAlignment(g187,g189)
    c: InternalAlignment(g188,g189)
    c: InternalAlignment(g190,g189)
    c: InternalAlignment(g191,g189)
    c: Weight(g192) = 1
    c: Equal(g192,g193)
    c: Equal(g192,g194)
    c: InternalAlignment(g192,g195)
    c: InternalAlignment(g193,g195)
    c: InternalAlignment(g194,g195)
    c: InternalAlignment(g196,g195)
    c: InternalAlignment(g197,g195)
    c: Weight(g198) = 1
    c: Equal(g198,g199)
    c: Equal(g198,g200)
    c: InternalAlignment(g198,g201)
    c: InternalAlignment(g199,g201)
    c: InternalAlignment(g200,g201)
    c: InternalAlignment(g202,g201)
    c: InternalAlignment(g203,g201)
    c: Block(g201)
    c: Block(g195)
    c: Block(g189)
    c: Block(g183)
    c: Coincident(g204,g201)
    c: Coincident(g204,g195)
    c: Horizontal(g204)
    c: Coincident(g205,g195)
    c: Coincident(g205,g25)
    c: Vertical(g205)
    c: Coincident(g206,g31)
    c: Coincident(g206,g189)
    c: Vertical(g206)
    c: Coincident(g207,g189)
    c: Coincident(g207,g183)
    c: Horizontal(g207)
    c: Coincident(g208,g183)
    c: Coincident(g208,g31)
    c: Coincident(g209,g25)
    c: Weight(g210) = 1
    c: Equal(g210,g211)
    c: Equal(g210,g212)
    c: InternalAlignment(g210,g213)
    c: InternalAlignment(g211,g213)
    c: InternalAlignment(g212,g213)
    c: InternalAlignment(g214,g213)
    c: InternalAlignment(g215,g213)
    c: Weight(g216) = 1
    c: Equal(g216,g217)
    c: Equal(g216,g218)
    c: InternalAlignment(g216,g219)
    c: InternalAlignment(g217,g219)
    c: InternalAlignment(g218,g219)
    c: InternalAlignment(g220,g219)
    c: InternalAlignment(g221,g219)
    c: Block(g219)
    c: Block(g213)
    c: Coincident(g222,g219)
    c: Coincident(g222,g49)
    c: Coincident(g223,g49)
    c: Coincident(g223,g213)
    c: Coincident(g224,g213)
    c: Coincident(g224,g219)
    c: Vertical(g224)
    c: Weight(g225) = 1
    c: Equal(g225,g226)
    c: Equal(g225,g227)
    c: InternalAlignment(g225,g228)
    c: InternalAlignment(g226,g228)
    c: InternalAlignment(g227,g228)
    c: InternalAlignment(g229,g228)
    c: InternalAlignment(g230,g228)
    c: Weight(g231) = 1
    c: Equal(g231,g232)
    c: Equal(g231,g233)
    c: InternalAlignment(g231,g234)
    c: InternalAlignment(g232,g234)
    c: InternalAlignment(g233,g234)
    c: InternalAlignment(g235,g234)
    c: InternalAlignment(g236,g234)
    c: Block(g234)
    c: Block(g228)
    c: Coincident(g237,g228)
    c: Coincident(g237,g55)
    c: Coincident(g238,g55)
    c: Coincident(g238,g234)
    c: Coincident(g239,g234)
    c: Coincident(g239,g228)
    c: Vertical(g239)
    c: Horizontal(g240)
    c: Block(g240)
    c: Vertical(g241)
    c: Block(g241)
    c: Block(g242)
    c: Weight(g243) = 1
    c: Equal(g243,g244)
    c: Equal(g243,g245)
    c: InternalAlignment(g243,g246)
    c: InternalAlignment(g244,g246)
    c: InternalAlignment(g245,g246)
    c: InternalAlignment(g247,g246)
    c: InternalAlignment(g248,g246)
    c: Weight(g249) = 1
    c: Equal(g249,g250)
    c: Equal(g249,g251)
    c: InternalAlignment(g249,g252)
    c: InternalAlignment(g250,g252)
    c: InternalAlignment(g251,g252)
    c: InternalAlignment(g253,g252)
    c: InternalAlignment(g254,g252)
    c: Weight(g255) = 1
    c: Equal(g255,g256)
    c: Equal(g255,g257)
    c: InternalAlignment(g255,g258)
    c: InternalAlignment(g256,g258)
    c: InternalAlignment(g257,g258)
    c: InternalAlignment(g259,g258)
    c: InternalAlignment(g260,g258)
    c: Weight(g261) = 1
    c: Equal(g261,g262)
    c: Equal(g261,g263)
    c: InternalAlignment(g261,g264)
    c: InternalAlignment(g262,g264)
    c: InternalAlignment(g263,g264)
    c: InternalAlignment(g265,g264)
    c: InternalAlignment(g266,g264)
    c: Block(g246)
    c: Block(g252)
    c: Block(g258)
    c: Block(g264)
    c: Coincident(g267,g252)
    c: Coincident(g267,g246)
    c: Horizontal(g267)
    c: Block(g209)
    c: Horizontal(g268)
    c: Vertical(g269)
    c: Horizontal(g270)
    c: Vertical(g271)
    c: Vertical(g272)
    c: Vertical(g275)
FEATURE [Sketcher::SketchObject] Sketch001
  FullyConstrained = true
  MapMode = 4
  Placement = pos=(0,0,0) rot=(0.57735,0.57735,0.57735;2.0944rad)
  Support = -> [Sketch]
  sketch-geometry (46):
    g0: BSplineCurve PolesCount=3 KnotsCount=2 Degree=2 IsPeriodic=0
    g1: ArcOfCircle CenterX=73.1223 CenterY=-32.291 CenterZ=0 NormalX=0 NormalY=0 NormalZ=1 AngleXU=0 Radius=13 StartAngle=5.92268 EndAngle=9.06428
    g2: ArcOfCircle CenterX=66.7816 CenterY=-49.1439 CenterZ=0 NormalX=0 NormalY=0 NormalZ=1 AngleXU=0 Radius=13 StartAngle=2.78068 EndAngle=5.92131
    g3: ArcOfCircle CenterX=55.9263 CenterY=-78.1807 CenterZ=0 NormalX=0 NormalY=0 NormalZ=1 AngleXU=0 Radius=13 StartAngle=5.92268 EndAngle=9.06428
    g4: ArcOfCircle CenterX=49.5884 CenterY=-95.0342 CenterZ=0 NormalX=0 NormalY=0 NormalZ=1 AngleXU=0 Radius=13 StartAngle=2.78068 EndAngle=5.92131
    g5: ArcOfCircle CenterX=38.7206 CenterY=-124.067 CenterZ=0 NormalX=0 NormalY=0 NormalZ=1 AngleXU=0 Radius=13 StartAngle=5.92268 EndAngle=9.06428
    g6: ArcOfCircle CenterX=32.3875 CenterY=-140.92 CenterZ=0 NormalX=0 NormalY=0 NormalZ=1 AngleXU=0 Radius=13 StartAngle=2.78068 EndAngle=5.92131
    g7: ArcOfCircle CenterX=21.4715 CenterY=-169.934 CenterZ=0 NormalX=0 NormalY=0 NormalZ=1 AngleXU=0 Radius=13 StartAngle=5.92268 EndAngle=9.06428
    g8: ArcOfCircle CenterX=15.1336 CenterY=-186.787 CenterZ=0 NormalX=0 NormalY=0 NormalZ=1 AngleXU=0 Radius=13 StartAngle=2.78068 EndAngle=5.92131
    g9-g12: Circle x4 (B-spline internal-alignment scaffolding for g13; pole/knot coordinates omitted)
    g13: BSplineCurve PolesCount=4 KnotsCount=2 Degree=3 IsPeriodic=0
    g14: GeomPoint X=28.8094 Y=-19.0875 Z=0
    g15: GeomPoint X=47.0443 Y=-50.4712 Z=0
    g16: Circle CenterX=53.5586 CenterY=-23.2695 CenterZ=0 NormalX=0 NormalY=0 NormalZ=1 AngleXU=0 Radius=3.24518
    g17: Circle CenterX=-195.441 CenterY=-127.082 CenterZ=0 NormalX=0 NormalY=0 NormalZ=1 AngleXU=0 Radius=1
    g18: Circle CenterX=-8.24091 CenterY=-197.481 CenterZ=0 NormalX=0 NormalY=0 NormalZ=1 AngleXU=0 Radius=1
    g19: Circle CenterX=12.8789 CenterY=-141.321 CenterZ=0 NormalX=0 NormalY=0 NormalZ=1 AngleXU=0 Radius=1
    g20: BSplineCurve PolesCount=3 KnotsCount=2 Degree=2 IsPeriodic=0
    g21: GeomPoint X=-195.441 Y=-127.082 Z=0
    g22: GeomPoint X=12.8789 Y=-141.321 Z=0
    g23: Circle CenterX=-12.8016 CenterY=-179.036 CenterZ=0 NormalX=0 NormalY=0 NormalZ=1 AngleXU=0 Radius=10.5072
    g24: Circle CenterX=0.933922 CenterY=-166.43 CenterZ=0 NormalX=0 NormalY=0 NormalZ=1 AngleXU=0 Radius=3.26661
    g25: Circle CenterX=-33.5518 CenterY=-176.44 CenterZ=0 NormalX=0 NormalY=0 NormalZ=1 AngleXU=0 Radius=5.64388
    g26: Circle CenterX=-47.2366 CenterY=-173.859 CenterZ=0 NormalX=0 NormalY=0 NormalZ=1 AngleXU=0 Radius=3.01653
    g27: Circle CenterX=-56.2595 CenterY=-171.456 CenterZ=0 NormalX=0 NormalY=0 NormalZ=1 AngleXU=0 Radius=2.12826
    g28: ArcOfCircle CenterX=51.2151 CenterY=-198.473 CenterZ=0 NormalX=0 NormalY=0 NormalZ=1 AngleXU=0 Radius=20 StartAngle=2.78189 EndAngle=4.35269
    g29: LineSegment StartX=32.4951 StartY=-191.433 StartZ=0 EndX=94.6578 EndY=-26.1352 EndZ=0
    g30: LineSegment StartX=43.1192 StartY=-220.001 StartZ=0 EndX=-196.497 EndY=-129.89 EndZ=0
    g31: LineSegment StartX=43.1192 StartY=-220.001 StartZ=0 EndX=44.1752 EndY=-217.193 EndZ=0
    g32: LineSegment StartX=117.223 StartY=-19.0875 StartZ=0 EndX=117.223 EndY=-16.0875 EndZ=0
    g33: LineSegment StartX=117.223 StartY=-16.0875 StartZ=0 EndX=17.2232 EndY=-16.0875 EndZ=0
    g34: LineSegment StartX=17.2232 StartY=-16.0875 StartZ=0 EndX=17.2232 EndY=-19.0875 EndZ=0
    g35: LineSegment StartX=28.8094 StartY=-19.0875 StartZ=0 EndX=17.2232 EndY=-19.0875 EndZ=0
    g36: LineSegment StartX=47.0443 StartY=-50.4712 StartZ=0 EndX=12.8789 EndY=-141.321 EndZ=0
    g37: LineSegment StartX=-195.441 StartY=-127.082 StartZ=0 EndX=-196.497 EndY=-129.89 EndZ=0
    g38: LineSegment StartX=85.2866 StartY=-36.8766 StartZ=0 EndX=78.9396 EndY=-53.7463 EndZ=0
    g39: LineSegment StartX=60.9579 StartY=-27.7053 StartZ=0 EndX=54.6191 EndY=-44.5532 EndZ=0
    g40: LineSegment StartX=68.0907 StartY=-82.7664 StartZ=0 EndX=61.7465 EndY=-99.6365 EndZ=0
    g41: LineSegment StartX=43.7619 StartY=-73.595 StartZ=0 EndX=37.426 EndY=-90.4435 EndZ=0
    g42: LineSegment StartX=50.885 StartY=-128.652 StartZ=0 EndX=44.5456 EndY=-145.522 EndZ=0
    g43: LineSegment StartX=26.5562 StartY=-119.481 StartZ=0 EndX=20.2251 EndY=-136.329 EndZ=0
    g44: LineSegment StartX=9.3071 StartY=-165.349 StartZ=0 EndX=2.97115 EndY=-182.197 EndZ=0
    g45: LineSegment StartX=33.6358 StartY=-174.52 StartZ=0 EndX=27.2917 EndY=-191.39 EndZ=0
  constraints (71):
    c: Block(g0)
    c: Block(g1)
    c: Block(g2)
    c: Block(g4)
    c: Block(g3)
    c: Block(g6)
    c: Block(g5)
    c: Block(g8)
    c: Block(g7)
    c: Weight(g9) = 1
    c: Equal(g9,g10)
    c: Equal(g9,g11)
    c: Equal(g9,g12)
    c: InternalAlignment(g9-g12 -> g13) x4
    c: InternalAlignment(g14,g13)
    c: InternalAlignment(g15,g13)
    c: Block(g16)
    c: Weight(g17) = 1
    c: Equal(g17,g18)
    c: Equal(g17,g19)
    c: InternalAlignment(g17,g20)
    c: InternalAlignment(g18,g20)
    c: InternalAlignment(g19,g20)
    c: InternalAlignment(g21,g20)
    c: InternalAlignment(g22,g20)
    c: Block(g20)
    c: Block(g23)
    c: Block(g24)
    c: Block(g25)
    c: Block(g26)
    c: Block(g27)
    c: Block(g28)
    c: Coincident(g29,g28)
    c: Coincident(g29,g0)
    c: Block(g13)
    c: Coincident(g31,g30)
    c: Coincident(g31,g28)
    c: Block(g31)
    c: Coincident(g32,g0)
    c: Vertical(g32)
    c: Coincident(g33,g32)
    c: Horizontal(g33)
    c: Coincident(g34,g33)
    c: Vertical(g34)
    c: Block(g33)
    c: Coincident(g35,g13)
    c: Coincident(g35,g34)
    c: Horizontal(g35)
    c: Coincident(g36,g13)
    c: Coincident(g36,g20)
    c: Coincident(g37,g20)
    c: Coincident(g37,g30)
    c: Block(g30)
    c: Coincident(g38,g1)
    c: Coincident(g38,g2)
    c: Coincident(g39,g1)
    c: Coincident(g39,g2)
    c: Coincident(g40,g3)
    c: Coincident(g40,g4)
    c: Coincident(g41,g3)
    c: Coincident(g41,g4)
    c: Coincident(g42,g5)
    c: Coincident(g42,g6)
    c: Coincident(g43,g5)
    c: Coincident(g43,g6)
    c: Coincident(g44,g7)
    c: Coincident(g44,g8)
    c: Coincident(g45,g7)
    c: Coincident(g45,g8)
    c: Distance(g30) = 256
    c: Distance(g33) = 100
FEATURE [Part::Extrusion] Extrude002
  Base = -> Sketch001
  Dir = (1,0,0)
  DirMode = 2
  FaceMakerClass = Part::FaceMakerBullseye
  LengthFwd = 8
  LengthRev = 0
  Solid = true
  Symmetric = false
FEATURE [Sketcher::SketchObject] Sketch002
  FullyConstrained = true
  sketch-geometry (20):
    g0: LineSegment StartX=-2.77179 StartY=-200.304 StartZ=0 EndX=5.22821 EndY=-200.304 EndZ=0
    g1: LineSegment StartX=5.22821 StartY=-200.304 StartZ=0 EndX=5.22821 EndY=-197.304 EndZ=0
    g2: LineSegment StartX=-2.77179 StartY=-200.304 StartZ=0 EndX=-2.77179 EndY=-197.304 EndZ=0
    g3: LineSegment StartX=5.22821 StartY=-197.304 StartZ=0 EndX=8.22821 EndY=-197.304 EndZ=0
    g4: LineSegment StartX=-2.77179 StartY=-197.304 StartZ=0 EndX=-5.77179 EndY=-197.304 EndZ=0
    g5: LineSegment StartX=19.2282 StartY=-203.304 StartZ=0 EndX=19.2282 EndY=-206.304 EndZ=0
    g6: LineSegment StartX=-16.7718 StartY=-203.304 StartZ=0 EndX=-16.7718 EndY=-206.304 EndZ=0
    g7: LineSegment StartX=-16.7718 StartY=-206.304 StartZ=0 EndX=19.2282 EndY=-206.304 EndZ=0
    g8: Circle CenterX=-16.7718 CenterY=-203.304 CenterZ=0 NormalX=0 NormalY=0 NormalZ=1 AngleXU=0 Radius=1
    g9: Circle CenterX=-5.77179 CenterY=-203.304 CenterZ=0 NormalX=0 NormalY=0 NormalZ=1 AngleXU=0 Radius=1
    g10: Circle CenterX=-5.77179 CenterY=-197.304 CenterZ=0 NormalX=0 NormalY=0 NormalZ=1 AngleXU=0 Radius=1
    g11: BSplineCurve PolesCount=3 KnotsCount=2 Degree=2 IsPeriodic=0
    g12: GeomPoint X=-16.7718 Y=-203.304 Z=0
    g13: GeomPoint X=-5.77179 Y=-197.304 Z=0
    g14: Circle CenterX=19.2282 CenterY=-203.304 CenterZ=0 NormalX=0 NormalY=0 NormalZ=1 AngleXU=0 Radius=1
    g15: Circle CenterX=8.22821 CenterY=-203.304 CenterZ=0 NormalX=0 NormalY=0 NormalZ=1 AngleXU=0 Radius=1
    g16: Circle CenterX=8.22821 CenterY=-197.304 CenterZ=0 NormalX=0 NormalY=0 NormalZ=1 AngleXU=0 Radius=1
    g17: BSplineCurve PolesCount=3 KnotsCount=2 Degree=2 IsPeriodic=0
    g18: GeomPoint X=19.2282 Y=-203.304 Z=0
    g19: GeomPoint X=8.22821 Y=-197.304 Z=0
  constraints (41):
    c: Horizontal(g0)
    c: Distance(g0) = 8
    c: Coincident(g1,g0)
    c: Vertical(g1)
    c: Distance(g1) = 3
    c: Coincident(g2,g0)
    c: Vertical(g2)
    c: Distance(g2) = 3
    c: Coincident(g3,g1)
    c: Horizontal(g3)
    c: Distance(g3) = 3
    c: Coincident(g4,g2)
    c: Horizontal(g4)
    c: Distance(g4) = 3
    c: Vertical(g5)
    c: Vertical(g6)
    c: Coincident(g7,g6)
    c: Coincident(g7,g5)
    c: Weight(g8) = 1
    c: Equal(g8,g9)
    c: Equal(g8,g10)
    c: Coincident(g11,g4)
    c: InternalAlignment(g8,g11)
    c: InternalAlignment(g9,g11)
    c: InternalAlignment(g10,g11)
    c: InternalAlignment(g12,g11)
    c: InternalAlignment(g13,g11)
    c: Coincident(g17,g5)
    c: Weight(g14) = 1
    c: Equal(g14,g15)
    c: Equal(g14,g16)
    c: Coincident(g17,g3)
    c: InternalAlignment(g14,g17)
    c: InternalAlignment(g15,g17)
    c: InternalAlignment(g16,g17)
    c: InternalAlignment(g18,g17)
    c: InternalAlignment(g19,g17)
    c: Block(g7)
    c: Block(g17)
    c: Block(g11)
    c: Block(g6)
FEATURE [Part::Extrusion] Extrude003
  Base = -> Sketch002
  Dir = (0,0,1)
  DirMode = 2
  FaceMakerClass = Part::FaceMakerBullseye
  LengthFwd = 260
  LengthRev = 0
  Solid = true
  Symmetric = false
FEATURE [Part::Extrusion] Extrude
  Base = -> Sketch
  Dir = (0,0,1)
  DirMode = 2
  FaceMakerClass = Part::FaceMakerBullseye
  LengthFwd = 14
  LengthRev = 0
  Solid = true
  Symmetric = false
